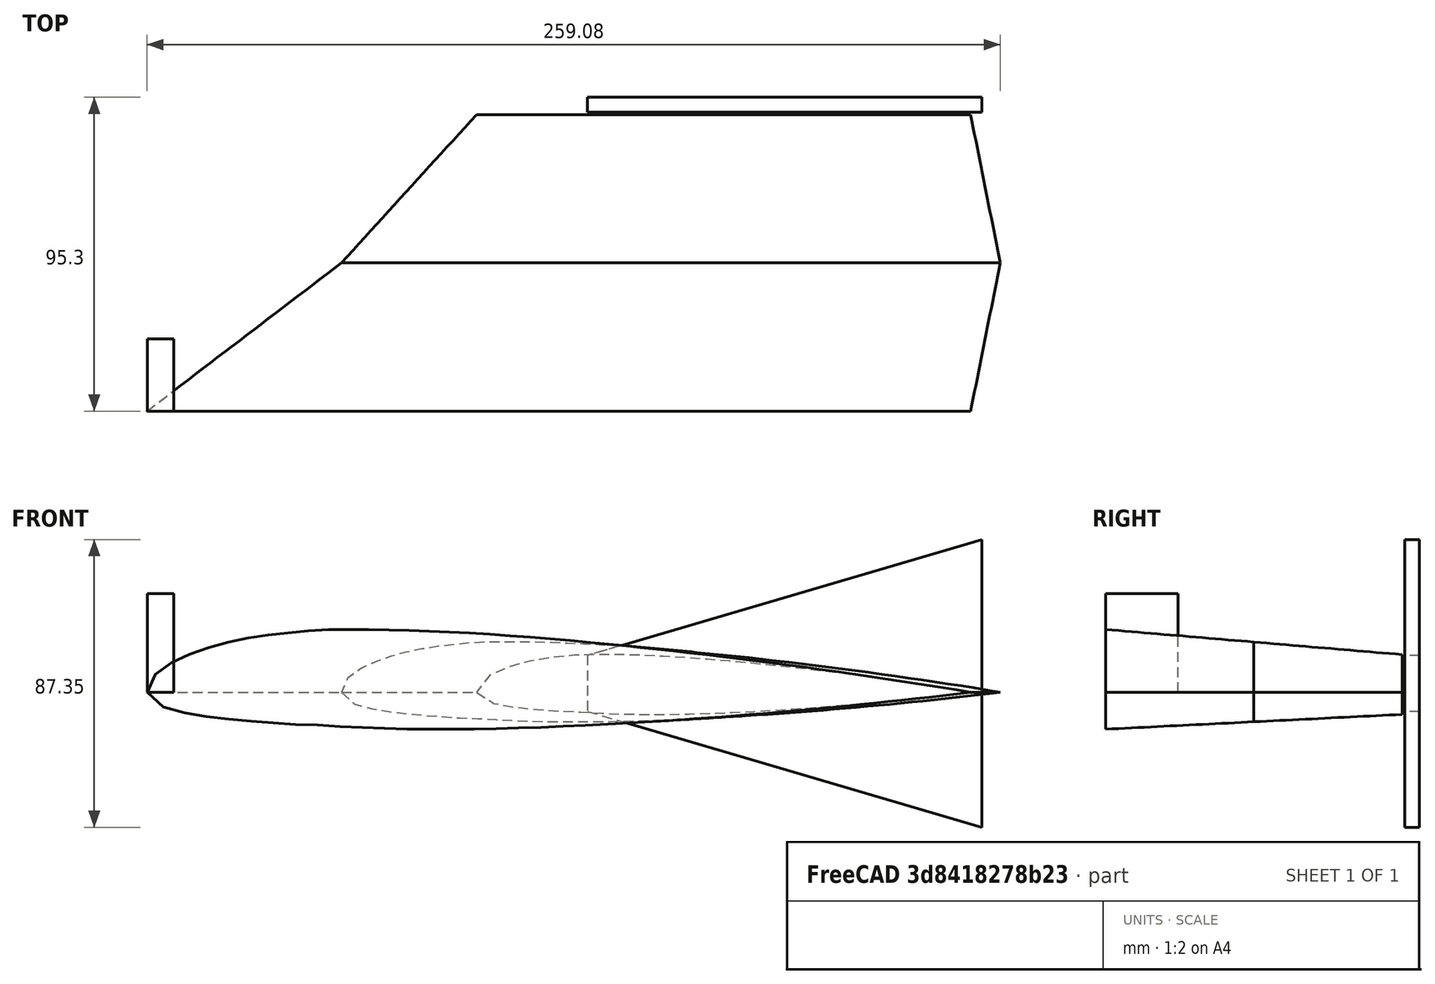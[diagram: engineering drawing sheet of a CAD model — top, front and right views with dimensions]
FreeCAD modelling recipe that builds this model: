
FCSTD DOCUMENT  (FreeCAD 0.20R29410 (Git))
Label: WingFem
License: All rights reserved
LicenseURL: http://en.wikipedia.org/wiki/All_rights_reserved
objects: Part::FeaturePython×3, Part::Loft×2, Sketcher::SketchObject×1, PartDesign::Pad×1, PartDesign::Body×1, Part::MultiFuse×1, Part::Box×1
note: 11 computed .brp shape members not serialized (recipe doc carries the construction recipe); baked Part::Feature solids carry a one-line shape summary decoded from their .brp

FEATURE [Part::FeaturePython] wrib  # WARN: FeaturePython — macro-defined, semantics opaque (R4)
  Chord = 250
  Coordinates = (101) [(1,0,-1.66492e-17),(0.99901,0,0.000165389),(0.996045,0,0.000659808),(0.991115,0,0.00147806),(0.984241,0,0.00261162),(0.97545,0,0.00404888),+95 more]
  NacaNbrPoint = 50
  NacaProfil = 24112
  RibProfil = 24112
  Thickness = 0
  finite_TE = false
  splitSpline = true
  useSpline = true
  wingkey = 0
FEATURE [Part::FeaturePython] wrib001  # WARN: FeaturePython — macro-defined, semantics opaque (R4)
  Chord = 200
  Coordinates = (101) [(1,0,-1.66492e-17),(0.99901,0,0.000165389),(0.996045,0,0.000659808),(0.991115,0,0.00147806),(0.984241,0,0.00261162),(0.97545,0,0.00404888),+95 more]
  NacaNbrPoint = 50
  NacaProfil = 24112
  Placement = pos=(59,45,0) rot=(1,0,0;0rad)
  RibProfil = 24112
  Thickness = 0
  finite_TE = false
  splitSpline = true
  useSpline = true
  wingkey = 0
FEATURE [Part::FeaturePython] wrib003  # WARN: FeaturePython — macro-defined, semantics opaque (R4)
  Chord = 150
  Coordinates = (101) [(1,0,-1.66492e-17),(0.99901,0,0.000165389),(0.996045,0,0.000659808),(0.991115,0,0.00147806),(0.984241,0,0.00261162),(0.97545,0,0.00404888),+95 more]
  NacaNbrPoint = 50
  NacaProfil = 24112
  Placement = pos=(100,90,0) rot=(1,0,0;0rad)
  RibProfil = 24112
  Thickness = 0
  finite_TE = false
  splitSpline = true
  useSpline = true
  wingkey = 0
FEATURE [Sketcher::SketchObject] Sketch001
  FullyConstrained = false
  MapMode = 5
  Placement = pos=(0,0,0) rot=(1,0,0;1.5708rad)
  Support = -> [XZ_Plane001]
  sketch-geometry (4):
    g0: LineSegment StartX=-116.313 StartY=11.1837 StartZ=0 EndX=-116.313 EndY=-5.83844 EndZ=0
    g1: LineSegment StartX=-116.313 StartY=-5.83844 StartZ=0 EndX=3.37282 EndY=-41.0031 EndZ=0
    g2: LineSegment StartX=3.37282 StartY=-41.0031 StartZ=0 EndX=3.37282 EndY=46.3483 EndZ=0
    g3: LineSegment StartX=3.37282 StartY=46.3483 StartZ=0 EndX=-116.313 EndY=11.1837 EndZ=0
  constraints (7):
    c: Vertical(g0)
    c: Coincident(g0,g1)
    c: Coincident(g1,g2)
    c: Vertical(g2)
    c: Coincident(g2,g3)
    c: Coincident(g3,g0)
    c: Equal(g3,g1)
FEATURE [PartDesign::Pad] Pad001
  Direction = (0,-1,2e-16)
  Length = 4.5
  Length2 = 10
  Placement = pos=(0,0,0) rot=(1,0,0;1.5708rad)
  Profile = -> Sketch001
  ReferenceAxis = -> Sketch001 [N_Axis]
  Type = 0
FEATURE [PartDesign::Body] Body001
  Group = -> [Sketch001,Pad001]
  Origin = -> Origin001
  Placement = pos=(250,95.3,0) rot=(0,0,1;0rad)
  Tip = -> Pad001
FEATURE [Part::Loft] Loft
  Closed = false
  MaxDegree = 5
  Ruled = false
  Sections = -> [wrib001,wrib003]
  Solid = true
FEATURE [Part::Loft] Loft001
  Closed = false
  MaxDegree = 5
  Ruled = false
  Sections = -> [wrib,wrib001]
  Solid = true
FEATURE [Part::MultiFuse] Fusion
  Shapes = -> [Loft,Loft001,Body001]
FEATURE [Part::Box] Box  label="envelope"
  AttacherType = Attacher::AttachEngine3D
  Height = 30
  Length = 8
  Width = 22
